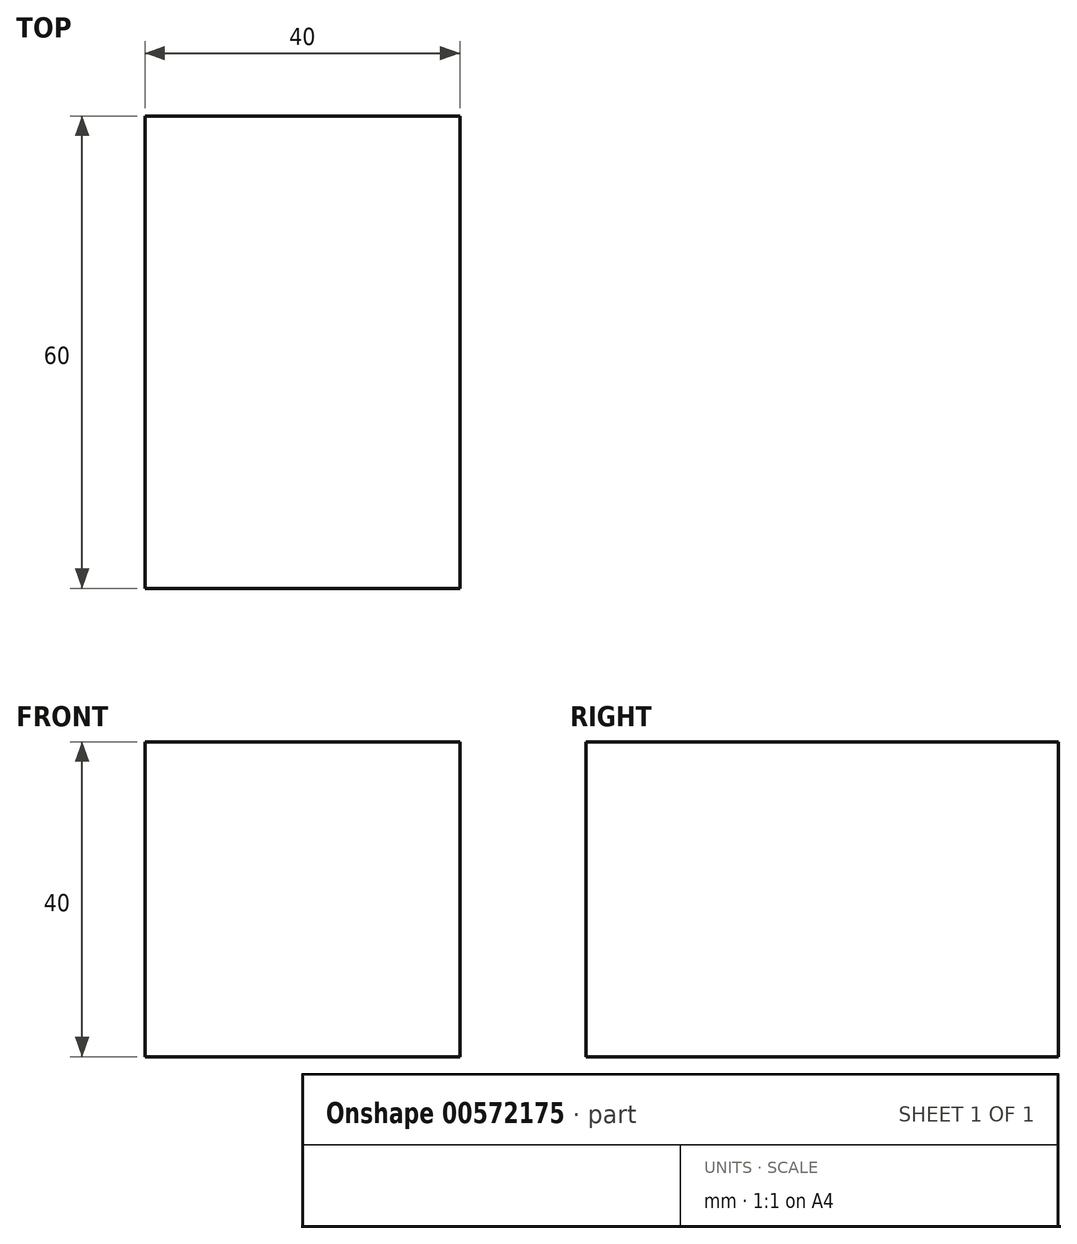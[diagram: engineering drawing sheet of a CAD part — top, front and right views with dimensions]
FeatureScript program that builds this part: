
annotation { "Feature Type Name" : "Feature", "Feature Type Description" : "" }
export const myFeature = defineFeature(function(context is Context, id is Id, definition is map)
    precondition{}
    {
        {
            var Q0;
            Q0=qCreatedBy(makeId("Top.planeOp"),FACE);
            var sketch = newSketch(context, id + "F0", { "sketchPlane" : qUnion([Q0])});
            skLineSegment(sketch, "E0.bottom", {"start": v(0, 0) * mm, "end": v(40, 0) * mm});
            skLineSegment(sketch, "E0.top", {"start": v(0, -60) * mm, "end": v(40, -60) * mm});
            skLineSegment(sketch, "E0.left", {"start": v(0, 0) * mm, "end": v(0, -60) * mm});
            skLineSegment(sketch, "E0.right", {"start": v(40, 0) * mm, "end": v(40, -60) * mm});
            skPoint(sketch, "E1.endSnap0", {"position": v(0, -30) * mm});
            skPoint(sketch, "E1.endSnap1", {"position": v(20, 0) * mm});
            skSolve(sketch);
        }
        {
            var Q0;
            Q0 = qSketchRegion(id + "F0", true);
            extrude(context, id + "F1", {"entities" : qUnion([Q0]), "depth" : 40 * mm, "offsetDistance" : 25 * mm});
        }
    });
